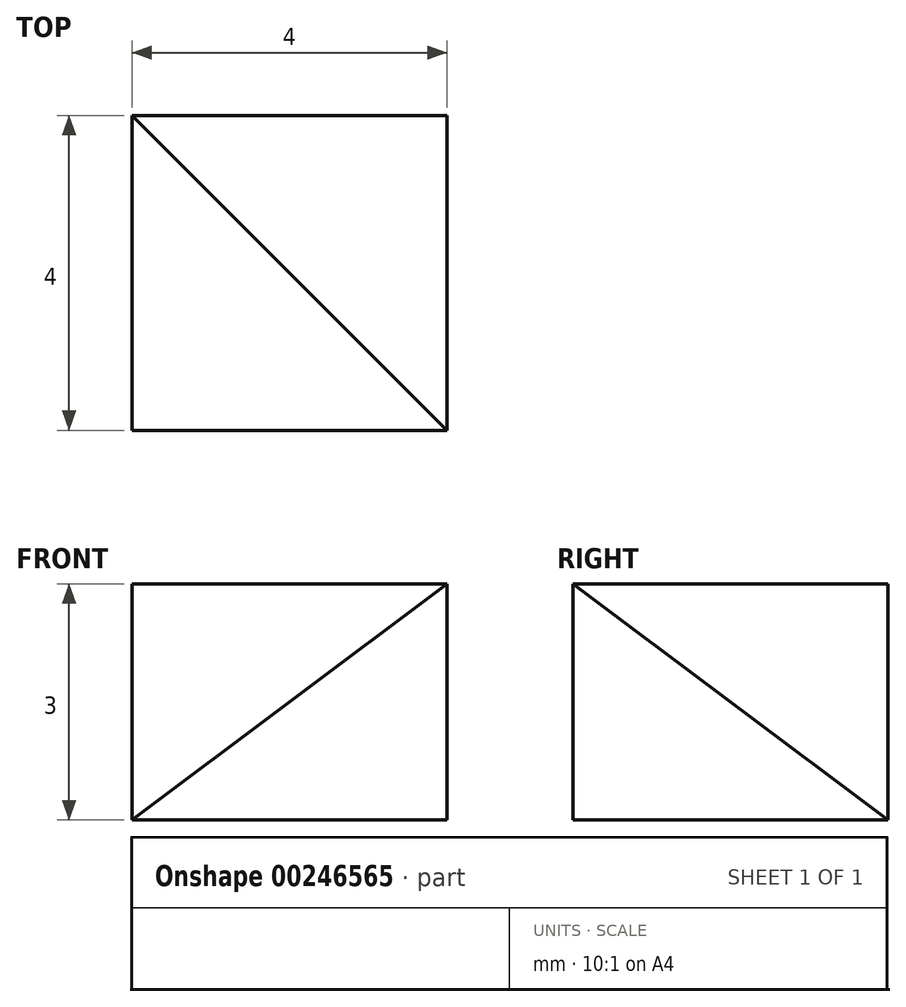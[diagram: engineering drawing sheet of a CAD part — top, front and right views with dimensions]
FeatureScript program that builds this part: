
annotation { "Feature Type Name" : "Feature", "Feature Type Description" : "" }
export const myFeature = defineFeature(function(context is Context, id is Id, definition is map)
    precondition{}
    {
        {
            var Q0;
            Q0=qCreatedBy(makeId("Top.planeOp"),FACE);
            var sketch = newSketch(context, id + "F0", { "sketchPlane" : qUnion([Q0])});
            skLineSegment(sketch, "E0.bottom", {"start": v(0, 0) * mm, "end": v(4, 0) * mm});
            skLineSegment(sketch, "E0.top", {"start": v(0, 4) * mm, "end": v(4, 4) * mm});
            skLineSegment(sketch, "E0.left", {"start": v(0, 0) * mm, "end": v(0, 4) * mm});
            skLineSegment(sketch, "E0.right", {"start": v(4, 0) * mm, "end": v(4, 4) * mm});
            skSolve(sketch);
        }
        {
            var Q0;
            Q0=makeQuery(id+"F0.imprint","IMPRINT",FACE,{"disambiguationData":[TD([[makeQuery(id+"F0.imprint","IMPRINT",EDGE,{"derivedFrom":sQuery(id+"F0.wireOp",EDGE,"E0.bottom")}),1.0]])]});
            extrude(context, id + "F1", {"entities" : qUnion([Q0]), "depth" : 3 * mm});
        }
        {
            var Q0;
            Q0=makeQuery(id+"F1.opExtrude","CAP_VERTEX",VERTEX,{"disambiguationData":[OSD([sQuery(id+"F0.wireOp",EDGE,"E0.top"),sQuery(id+"F0.wireOp",EDGE,"E0.left")])],"isStart":false});
            var Q1;
            Q1=makeQuery(id+"F1.opExtrude","CAP_VERTEX",VERTEX,{"disambiguationData":[OSD([sQuery(id+"F0.wireOp",EDGE,"E0.bottom"),sQuery(id+"F0.wireOp",EDGE,"E0.right")])],"isStart":false});
            var Q2;
            Q2=makeQuery(id+"F1.opExtrude","CAP_VERTEX",VERTEX,{"disambiguationData":[OSD([sQuery(id+"F0.wireOp",EDGE,"E0.top"),sQuery(id+"F0.wireOp",EDGE,"E0.right")])],"isStart":true});
            cPlane(context, id + "F2", {"entities" : qUnion([Q0, Q1, Q2]), "cplaneType" : CPlaneType.THREE_POINT, "offset" : 25 * mm, "width" : 150 * mm, "height" : 150 * mm});
        }
        {
            var Q0;
            Q0=qCreatedBy(id+"F2.planeOp",FACE);
            var sketch = newSketch(context, id + "F3", { "sketchPlane" : qUnion([Q0])});
            skPoint(sketch, "E1.0", {"position": v(-2.47, -1.4) * mm});
            skPoint(sketch, "E1.1", {"position": v(2.2, -3.2) * mm});
            skPoint(sketch, "E1.2", {"position": v(2.2, 1.8) * mm});
            skLineSegment(sketch, "E2", {"start": v(2.2, 1.8) * mm, "end": v(-2.47, -1.4) * mm});
            skLineSegment(sketch, "E3", {"start": v(2.2, 1.8) * mm, "end": v(2.2, -3.2) * mm});
            skLineSegment(sketch, "E4", {"start": v(2.2, -3.2) * mm, "end": v(-2.47, -1.4) * mm});
            skSolve(sketch);
        }
        {
            var Q0;
            Q0 = qSketchRegion(id + "F3", true);
            extrude(context, id + "F4", {"entities" : qUnion([Q0]), "operationType" : NewBodyOperationType.REMOVE, "oppositeDirection" : true, "depth" : 25 * mm});
        }
        {
            var Q0;
            Q0=makeQuery(id+"F4.boolean.opBoolean","MERGE",VERTEX,{"derivedFrom":[makeQuery(id+"F1.opExtrude","CAP_VERTEX",VERTEX,{"disambiguationData":[OSD([sQuery(id+"F0.wireOp",EDGE,"E0.bottom"),sQuery(id+"F0.wireOp",EDGE,"E0.right")])],"isStart":false}),makeQuery(id+"F4.opExtrude","CAP_VERTEX",VERTEX,{"disambiguationData":[OSD([sQuery(id+"F3.wireOp",EDGE,"E2"),sQuery(id+"F3.wireOp",EDGE,"E3")])],"isStart":true})]});
            var Q1;
            Q1=makeQuery(id+"F4.boolean.opBoolean","MERGE",VERTEX,{"derivedFrom":[makeQuery(id+"F1.opExtrude","CAP_VERTEX",VERTEX,{"disambiguationData":[OSD([sQuery(id+"F0.wireOp",EDGE,"E0.top"),sQuery(id+"F0.wireOp",EDGE,"E0.left")])],"isStart":false}),makeQuery(id+"F4.opExtrude","CAP_VERTEX",VERTEX,{"disambiguationData":[OSD([sQuery(id+"F3.wireOp",EDGE,"E2"),sQuery(id+"F3.wireOp",EDGE,"E4")])],"isStart":true})]});
            var Q2;
            Q2=qCreatedBy(makeId("Origin.pointOp"),VERTEX);
            cPlane(context, id + "F5", {"entities" : qUnion([Q0, Q1, Q2]), "cplaneType" : CPlaneType.THREE_POINT, "offset" : 25 * mm, "width" : 150 * mm, "height" : 150 * mm});
        }
        {
            var Q0;
            Q0=qCreatedBy(id+"F5.planeOp",FACE);
            var sketch = newSketch(context, id + "F6", { "sketchPlane" : qUnion([Q0])});
            skPoint(sketch, "E5.0", {"position": v(0, -5) * mm});
            skPoint(sketch, "E5.1", {"position": v(4.66, -1.8) * mm});
            skPoint(sketch, "E5.2", {"position": v(0, 0) * mm});
            skLineSegment(sketch, "E6", {"start": v(0, -5) * mm, "end": v(0, 0) * mm});
            skLineSegment(sketch, "E7", {"start": v(0, -5) * mm, "end": v(4.66, -1.8) * mm});
            skLineSegment(sketch, "E8", {"start": v(4.66, -1.8) * mm, "end": v(0, 0) * mm});
            skSolve(sketch);
        }
        {
            var Q0;
            Q0 = qSketchRegion(id + "F6", true);
            extrude(context, id + "F7", {"entities" : qUnion([Q0]), "operationType" : NewBodyOperationType.REMOVE, "oppositeDirection" : true, "depth" : 25 * mm});
        }
    });
